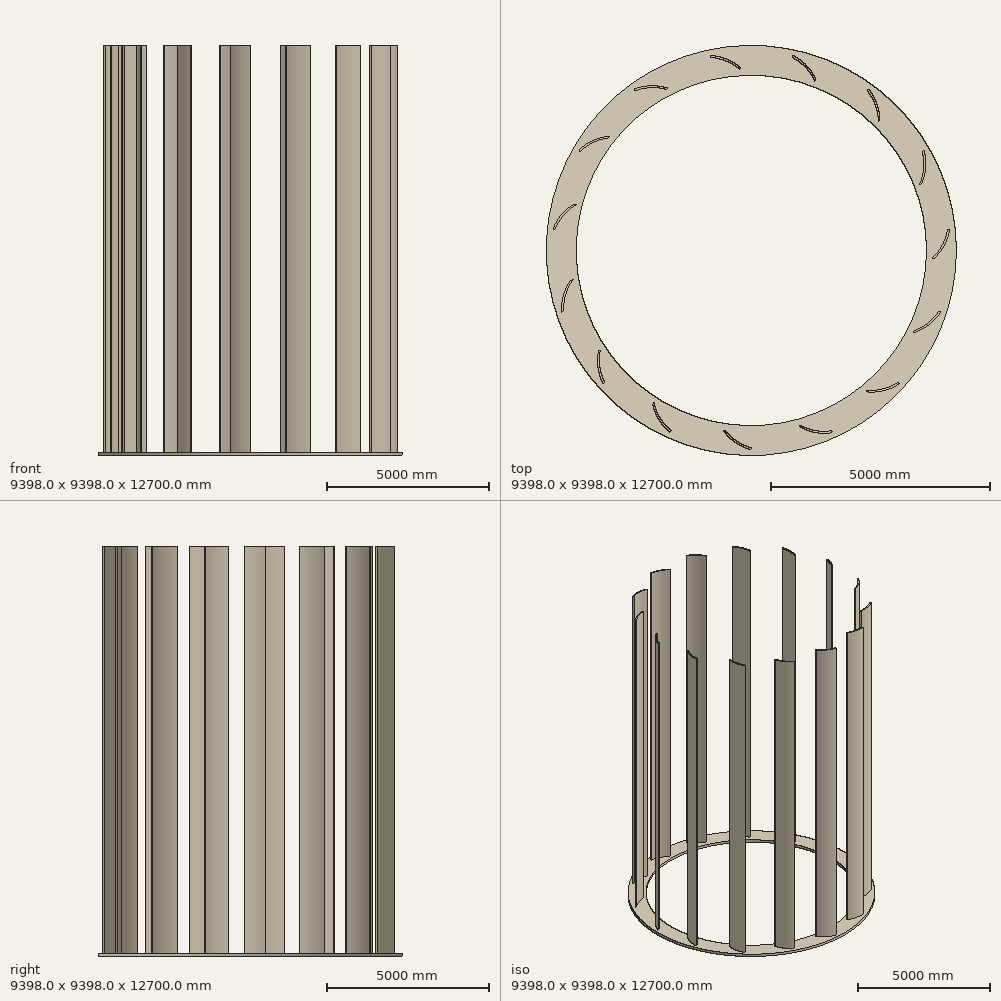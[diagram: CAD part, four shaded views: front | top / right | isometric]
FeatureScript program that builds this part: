
annotation { "Feature Type Name" : "Feature", "Feature Type Description" : "" }
export const myFeature = defineFeature(function(context is Context, id is Id, definition is map)
    precondition{}
    {
        {
            var Q0;
            Q0=qCreatedBy(makeId("Top.planeOp"),FACE);
            var sketch = newSketch(context, id + "F0", { "sketchPlane" : qUnion([Q0])});
            skCircle(sketch, "E0", {"center": v(0, 0) * mm, "radius": 4572 * mm, "construction": true});
            skLineSegment(sketch, "E1", {"start": v(4572, 0) * mm, "end": v(-4572, 0) * mm, "construction": true});
            skLineSegment(sketch, "E2", {"start": v(-3232.9, -3232.9) * mm, "end": v(3232.9, 3232.9) * mm, "construction": true});
            skLineSegment(sketch, "E3", {"start": v(0, -4572) * mm, "end": v(-630.02, -4143.38) * mm, "construction": true});
            skArc(sketch, "E4", {"start": v(-630.02, -4143.37) * mm, "mid": v(-351.78, -4411.73) * mm, "end": v(0, -4572) * mm});
            skLineSegment(sketch, "E5", {"start": v(-622.38, -4093.15) * mm, "end": v(0, -4521.2) * mm, "construction": true});
            skArc(sketch, "E6", {"start": v(-622.38, -4093.15) * mm, "mid": v(-347.57, -4360.08) * mm, "end": v(0, -4521.2) * mm});
            skLineSegment(sketch, "E7", {"start": v(-630.02, -4143.37) * mm, "end": v(-622.38, -4093.15) * mm});
            skLineSegment(sketch, "E8", {"start": v(0, -4572) * mm, "end": v(0, -4521.2) * mm});
            skArc(sketch, "E9.1.0", {"start": v(1109.71, -4041.41) * mm, "mid": v(1473.05, -4173.4) * mm, "end": v(1859.6, -4176.73) * mm});
            skArc(sketch, "E9.1.1", {"start": v(1096.26, -3992.43) * mm, "mid": v(1455.88, -4124.5) * mm, "end": v(1838.94, -4130.32) * mm});
            skArc(sketch, "E9.2.0", {"start": v(2657.56, -3240.65) * mm, "mid": v(3043.17, -3213.45) * mm, "end": v(3397.66, -3059.27) * mm});
            skArc(sketch, "E9.2.1", {"start": v(2625.35, -3201.37) * mm, "mid": v(3007.6, -3175.76) * mm, "end": v(3359.9, -3025.27) * mm});
            skArc(sketch, "E10.2.3.0", {"start": v(3745.9, -1879.56) * mm, "mid": v(4087.1, -1697.86) * mm, "end": v(4348.23, -1412.83) * mm});
            skArc(sketch, "E10.4.3.0", {"start": v(3700.5, -1856.77) * mm, "mid": v(4039.27, -1677.9) * mm, "end": v(4299.92, -1397.13) * mm});
            skArc(sketch, "E10.2.4.0", {"start": v(4186.53, -193.47) * mm, "mid": v(4424.34, 111.3) * mm, "end": v(4546.95, 477.9) * mm});
            skArc(sketch, "E10.4.4.0", {"start": v(4135.79, -191.12) * mm, "mid": v(4372.52, 110.08) * mm, "end": v(4496.43, 472.6) * mm});
            skArc(sketch, "E11.2.5.0", {"start": v(3903.28, 1526.07) * mm, "mid": v(3996.56, 1901.22) * mm, "end": v(3959.47, 2286) * mm});
            skArc(sketch, "E11.4.5.0", {"start": v(3855.97, 1507.58) * mm, "mid": v(3949.72, 1879.03) * mm, "end": v(3915.47, 2260.6) * mm});
            skArc(sketch, "E11.2.6.0", {"start": v(2945.11, 2981.74) * mm, "mid": v(2877.75, 3362.4) * mm, "end": v(2687.35, 3698.83) * mm});
            skArc(sketch, "E11.4.6.0", {"start": v(2909.41, 2945.6) * mm, "mid": v(2843.98, 3323.08) * mm, "end": v(2657.5, 3657.73) * mm});
            skArc(sketch, "E11.2.7.0", {"start": v(1477.7, 3921.84) * mm, "mid": v(1261.34, 4242.19) * mm, "end": v(950.57, 4472.1) * mm});
            skArc(sketch, "E11.4.7.0", {"start": v(1459.8, 3874.3) * mm, "mid": v(1246.49, 4192.53) * mm, "end": v(940.01, 4422.4) * mm});
            skArc(sketch, "E11.2.8.0", {"start": v(-245.2, 4183.82) * mm, "mid": v(-573.16, 4388.47) * mm, "end": v(-950.57, 4472.1) * mm});
            skArc(sketch, "E11.4.8.0", {"start": v(-242.23, 4133.1) * mm, "mid": v(-566.53, 4337.06) * mm, "end": v(-940.01, 4422.4) * mm});
            skArc(sketch, "E11.2.9.0", {"start": v(-1925.72, 3722.38) * mm, "mid": v(-2308.56, 3775.94) * mm, "end": v(-2687.35, 3698.83) * mm});
            skArc(sketch, "E11.4.9.0", {"start": v(-1902.38, 3677.26) * mm, "mid": v(-2281.6, 3731.67) * mm, "end": v(-2657.5, 3657.73) * mm});
            skArc(sketch, "E12.2.10.0", {"start": v(-3273.26, 2617.3) * mm, "mid": v(-3644.78, 2510.52) * mm, "end": v(-3959.47, 2286) * mm});
            skArc(sketch, "E12.4.10.0", {"start": v(-3233.58, 2585.58) * mm, "mid": v(-3602.15, 2481.05) * mm, "end": v(-3915.47, 2260.6) * mm});
            skArc(sketch, "E12.2.11.0", {"start": v(-4054.82, 1059.67) * mm, "mid": v(-4350.8, 811) * mm, "end": v(-4546.95, 477.9) * mm});
            skArc(sketch, "E12.4.11.0", {"start": v(-4005.67, 1046.82) * mm, "mid": v(-4299.86, 801.42) * mm, "end": v(-4496.43, 472.6) * mm});
            skArc(sketch, "E12.2.12.0", {"start": v(-4135.27, -681.19) * mm, "mid": v(-4304.51, -1028.74) * mm, "end": v(-4348.23, -1412.83) * mm});
            skArc(sketch, "E12.4.12.0", {"start": v(-4085.15, -672.93) * mm, "mid": v(-4254.08, -1016.78) * mm, "end": v(-4299.92, -1397.13) * mm});
            skArc(sketch, "E12.2.13.0", {"start": v(-3500.7, -2304.26) * mm, "mid": v(-3513.94, -2690.6) * mm, "end": v(-3397.66, -3059.27) * mm});
            skArc(sketch, "E12.4.13.0", {"start": v(-3458.26, -2276.33) * mm, "mid": v(-3472.74, -2659.16) * mm, "end": v(-3359.9, -3025.27) * mm});
            skArc(sketch, "E12.2.14.0", {"start": v(-2260.81, -3528.9) * mm, "mid": v(-2115.78, -3887.24) * mm, "end": v(-1859.6, -4176.73) * mm});
            skArc(sketch, "E12.4.14.0", {"start": v(-2233.41, -3486.13) * mm, "mid": v(-2090.93, -3841.76) * mm, "end": v(-1838.94, -4130.32) * mm});
            skLineSegment(sketch, "E13.1.0", {"start": v(1859.6, -4176.73) * mm, "end": v(1838.94, -4130.32) * mm});
            skLineSegment(sketch, "E13.1.3", {"start": v(1109.71, -4041.41) * mm, "end": v(1096.26, -3992.43) * mm});
            skLineSegment(sketch, "E13.2.0", {"start": v(3397.66, -3059.27) * mm, "end": v(3359.9, -3025.27) * mm});
            skLineSegment(sketch, "E13.2.3", {"start": v(2657.56, -3240.65) * mm, "end": v(2625.35, -3201.37) * mm});
            skLineSegment(sketch, "E13.3.0", {"start": v(4348.23, -1412.83) * mm, "end": v(4299.92, -1397.13) * mm});
            skLineSegment(sketch, "E13.3.3", {"start": v(3745.9, -1879.56) * mm, "end": v(3700.5, -1856.77) * mm});
            skLineSegment(sketch, "E13.4.0", {"start": v(4546.95, 477.9) * mm, "end": v(4496.43, 472.6) * mm});
            skLineSegment(sketch, "E13.4.3", {"start": v(4186.53, -193.47) * mm, "end": v(4135.79, -191.12) * mm});
            skLineSegment(sketch, "E13.5.0", {"start": v(3959.47, 2286) * mm, "end": v(3915.47, 2260.6) * mm});
            skLineSegment(sketch, "E13.5.3", {"start": v(3903.28, 1526.07) * mm, "end": v(3855.97, 1507.58) * mm});
            skLineSegment(sketch, "E13.6.0", {"start": v(2687.35, 3698.83) * mm, "end": v(2657.5, 3657.73) * mm});
            skLineSegment(sketch, "E13.6.3", {"start": v(2945.11, 2981.74) * mm, "end": v(2909.41, 2945.6) * mm});
            skLineSegment(sketch, "E13.7.0", {"start": v(950.57, 4472.1) * mm, "end": v(940.01, 4422.4) * mm});
            skLineSegment(sketch, "E13.7.3", {"start": v(1477.7, 3921.84) * mm, "end": v(1459.8, 3874.3) * mm});
            skLineSegment(sketch, "E13.8.0", {"start": v(-950.57, 4472.1) * mm, "end": v(-940.01, 4422.4) * mm});
            skLineSegment(sketch, "E13.8.3", {"start": v(-245.2, 4183.82) * mm, "end": v(-242.23, 4133.1) * mm});
            skLineSegment(sketch, "E13.9.0", {"start": v(-2687.35, 3698.83) * mm, "end": v(-2657.5, 3657.73) * mm});
            skLineSegment(sketch, "E13.9.3", {"start": v(-1925.72, 3722.38) * mm, "end": v(-1902.38, 3677.26) * mm});
            skLineSegment(sketch, "E13.10.0", {"start": v(-3959.47, 2286) * mm, "end": v(-3915.47, 2260.6) * mm});
            skLineSegment(sketch, "E13.10.3", {"start": v(-3273.26, 2617.3) * mm, "end": v(-3233.58, 2585.58) * mm});
            skLineSegment(sketch, "E13.11.0", {"start": v(-4546.95, 477.9) * mm, "end": v(-4496.43, 472.6) * mm});
            skLineSegment(sketch, "E13.11.3", {"start": v(-4054.82, 1059.67) * mm, "end": v(-4005.67, 1046.82) * mm});
            skLineSegment(sketch, "E13.12.0", {"start": v(-4348.23, -1412.83) * mm, "end": v(-4299.92, -1397.13) * mm});
            skLineSegment(sketch, "E13.12.3", {"start": v(-4135.27, -681.19) * mm, "end": v(-4085.15, -672.93) * mm});
            skLineSegment(sketch, "E13.13.0", {"start": v(-3397.66, -3059.27) * mm, "end": v(-3359.9, -3025.27) * mm});
            skLineSegment(sketch, "E13.13.3", {"start": v(-3500.7, -2304.26) * mm, "end": v(-3458.26, -2276.33) * mm});
            skLineSegment(sketch, "E13.14.0", {"start": v(-1859.6, -4176.73) * mm, "end": v(-1838.94, -4130.32) * mm});
            skLineSegment(sketch, "E13.14.3", {"start": v(-2260.81, -3528.9) * mm, "end": v(-2233.41, -3486.13) * mm});
            skSolve(sketch);
        }
        {
            var Q0;
            Q0 = qSketchRegion(id + "F0", true);
            var Q1;
            Q1=makeQuery(id+"F0.imprint","IMPRINT",FACE,{"disambiguationData":[TD([[makeQuery(id+"F0.imprint","IMPRINT",EDGE,{"derivedFrom":sQuery(id+"F0.wireOp",EDGE,"E4")}),1.0]])]});
            extrude(context, id + "F1", {"entities" : qUnion([Q0, Q1]), "depth" : 12700 * mm, "offsetDistance" : 25.4 * mm});
        }
        {
            var Q0;
            Q0=qCreatedBy(makeId("Top.planeOp"),FACE);
            var sketch = newSketch(context, id + "F2", { "sketchPlane" : qUnion([Q0])});
            skCircle(sketch, "E14", {"center": v(0, 0) * mm, "radius": 4699 * mm});
            skCircle(sketch, "E15", {"center": v(0, 0) * mm, "radius": 4013.2 * mm});
            skSolve(sketch);
        }
        {
            var Q0;
            Q0 = qSketchRegion(id + "F2", true);
            extrude(context, id + "F3", {"entities" : qUnion([Q0]), "depth" : 101.6 * mm, "offsetDistance" : 25.4 * mm});
        }
    });
